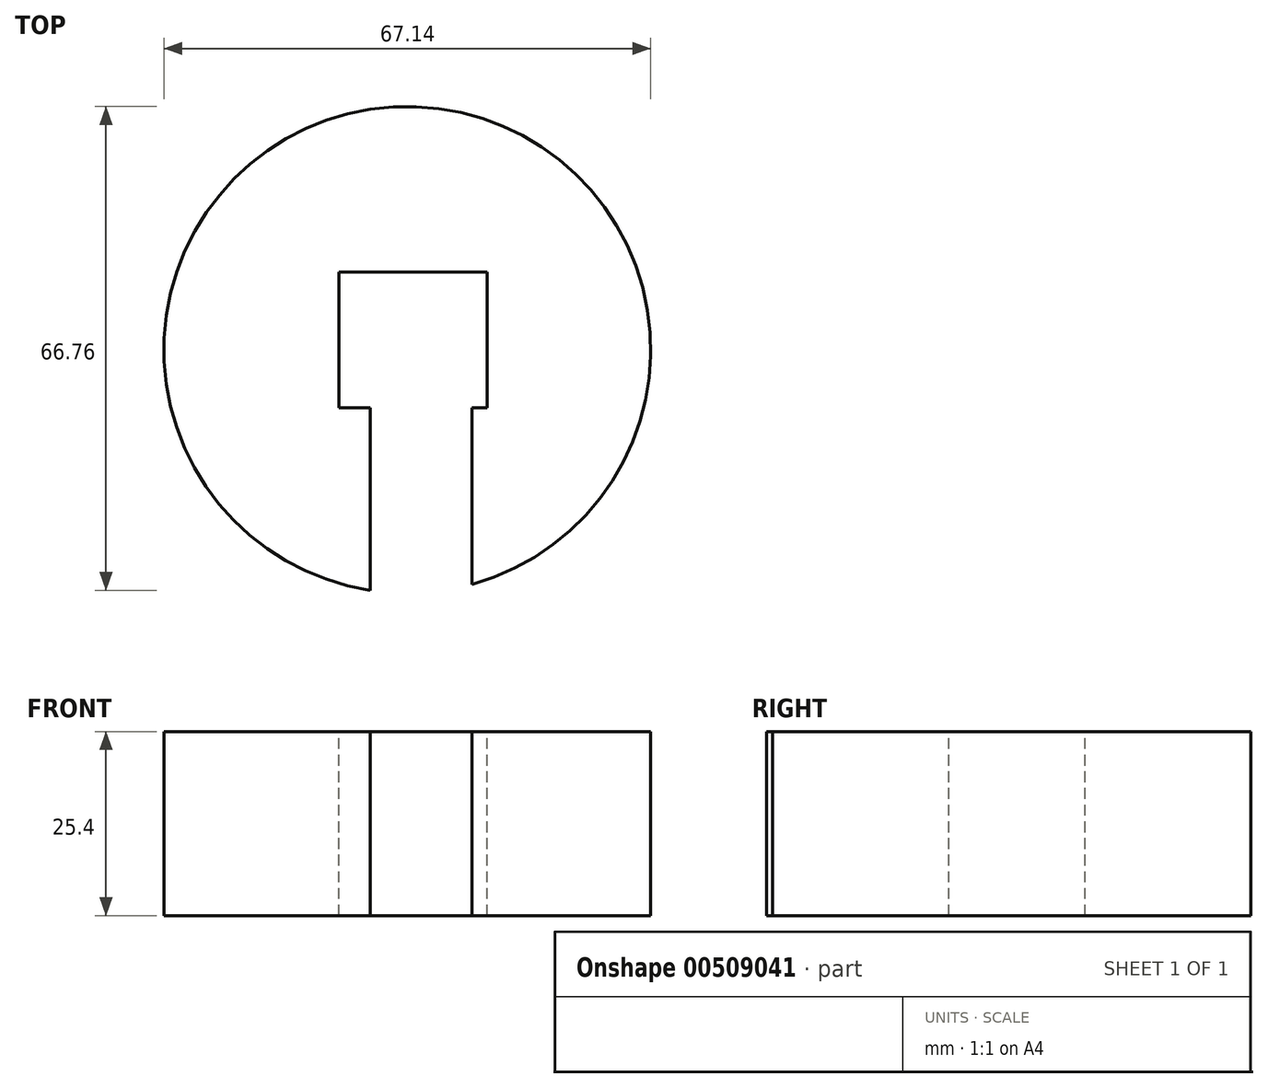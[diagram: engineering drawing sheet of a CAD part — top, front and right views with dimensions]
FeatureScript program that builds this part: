
annotation { "Feature Type Name" : "Feature", "Feature Type Description" : "" }
export const myFeature = defineFeature(function(context is Context, id is Id, definition is map)
    precondition{}
    {
        {
            var Q0;
            Q0=qCreatedBy(makeId("Top.planeOp"),FACE);
            var sketch = newSketch(context, id + "F0", { "sketchPlane" : qUnion([Q0])});
            skCircle(sketch, "E0", {"center": v(0, 33.57) * mm, "radius": 33.57 * mm});
            skSolve(sketch);
        }
        {
            var Q0;
            Q0=makeQuery(id+"F0.imprint","IMPRINT",FACE,{"disambiguationData":[TD([[makeQuery(id+"F0.imprint","IMPRINT",EDGE,{"derivedFrom":sQuery(id+"F0.wireOp",EDGE,"E0")}),1.0]])]});
            extrude(context, id + "F1", {"entities" : qUnion([Q0]), "depth" : 25.4 * mm});
        }
        {
            var Q0;
            Q0=qCreatedBy(makeId("Top.planeOp"),FACE);
            var sketch = newSketch(context, id + "F2", { "sketchPlane" : qUnion([Q0])});
            skLineSegment(sketch, "E1.bottom", {"start": v(-34.16, -26.92) * mm, "end": v(-64.95, -26.92) * mm});
            skLineSegment(sketch, "E1.top", {"start": v(-34.16, -55.67) * mm, "end": v(-64.95, -55.67) * mm});
            skLineSegment(sketch, "E1.left", {"start": v(-34.16, -26.92) * mm, "end": v(-34.16, -55.67) * mm});
            skLineSegment(sketch, "E1.right", {"start": v(-64.95, -26.92) * mm, "end": v(-64.95, -55.67) * mm});
            skSolve(sketch);
        }
        {
            var Q0;
            Q0=makeQuery(id+"F2.imprint","IMPRINT",FACE,{"disambiguationData":[TD([[makeQuery(id+"F2.imprint","IMPRINT",EDGE,{"derivedFrom":sQuery(id+"F2.wireOp",EDGE,"E1.bottom")}),1.0]])]});
            extrude(context, id + "F3", {"entities" : qUnion([Q0]), "depth" : 25.4 * mm});
        }
        {
            var Q0;
            Q0=makeQuery(id+"F3.opExtrude","SWEPT_BODY",BODY,{"disambiguationData":[OSD([sQuery(id+"F2.wireOp",EDGE,"E1.bottom"),sQuery(id+"F2.wireOp",EDGE,"E1.top"),sQuery(id+"F2.wireOp",EDGE,"E1.left"),sQuery(id+"F2.wireOp",EDGE,"E1.right")])]});
            deleteBodies(context, id + "F4", {"entities" : qUnion([Q0])});
        }
        {
            var Q0;
            Q0=makeQuery(id+"F1.opExtrude","CAP_FACE",FACE,{"disambiguationData":[OSD([sQuery(id+"F0.wireOp",EDGE,"E0")])],"isStart":false});
            var sketch = newSketch(context, id + "F5", { "sketchPlane" : qUnion([Q0])});
            skLineSegment(sketch, "E2.bottom", {"start": v(-9.45, 44.32) * mm, "end": v(11.02, 44.32) * mm});
            skLineSegment(sketch, "E2.top", {"start": v(-9.45, 25.54) * mm, "end": v(11.02, 25.54) * mm});
            skLineSegment(sketch, "E2.left", {"start": v(-9.45, 44.32) * mm, "end": v(-9.45, 25.54) * mm});
            skLineSegment(sketch, "E2.right", {"start": v(11.02, 44.32) * mm, "end": v(11.02, 25.54) * mm});
            skSolve(sketch);
        }
        {
            var Q0;
            Q0 = qSketchRegion(id + "F5", true);
            extrude(context, id + "F6", {"entities" : qUnion([Q0]), "operationType" : NewBodyOperationType.REMOVE, "oppositeDirection" : true, "depth" : 25.4 * mm});
        }
        {
            var Q0;
            Q0=makeQuery(id+"F1.opExtrude","CAP_FACE",FACE,{"disambiguationData":[OSD([sQuery(id+"F0.wireOp",EDGE,"E0")])],"isStart":false});
            var sketch = newSketch(context, id + "F7", { "sketchPlane" : qUnion([Q0])});
            skLineSegment(sketch, "E3.bottom", {"start": v(-5.09, 25.54) * mm, "end": v(8.95, 25.54) * mm});
            skLineSegment(sketch, "E3.top", {"start": v(-5.09, -4.94) * mm, "end": v(8.95, -4.94) * mm});
            skLineSegment(sketch, "E3.left", {"start": v(-5.09, 25.54) * mm, "end": v(-5.09, -4.94) * mm});
            skLineSegment(sketch, "E3.right", {"start": v(8.95, 25.54) * mm, "end": v(8.95, -4.94) * mm});
            skSolve(sketch);
        }
        {
            var Q0;
            Q0 = qSketchRegion(id + "F7", true);
            var Q1;
            {var subQ0=sQuery(id+"F7.wireOp",EDGE,"E3.bottom");Q1=makeQuery(id+"F7.imprint","IMPRINT",FACE,{"disambiguationData":[TD([[makeQuery(id+"F7.imprint","IMPRINT",EDGE,{"derivedFrom":subQ0}),-1.0]])]});}
            extrude(context, id + "F8", {"entities" : qUnion([Q0, Q1]), "operationType" : NewBodyOperationType.REMOVE, "oppositeDirection" : true, "depth" : 25.4 * mm});
        }
    });
